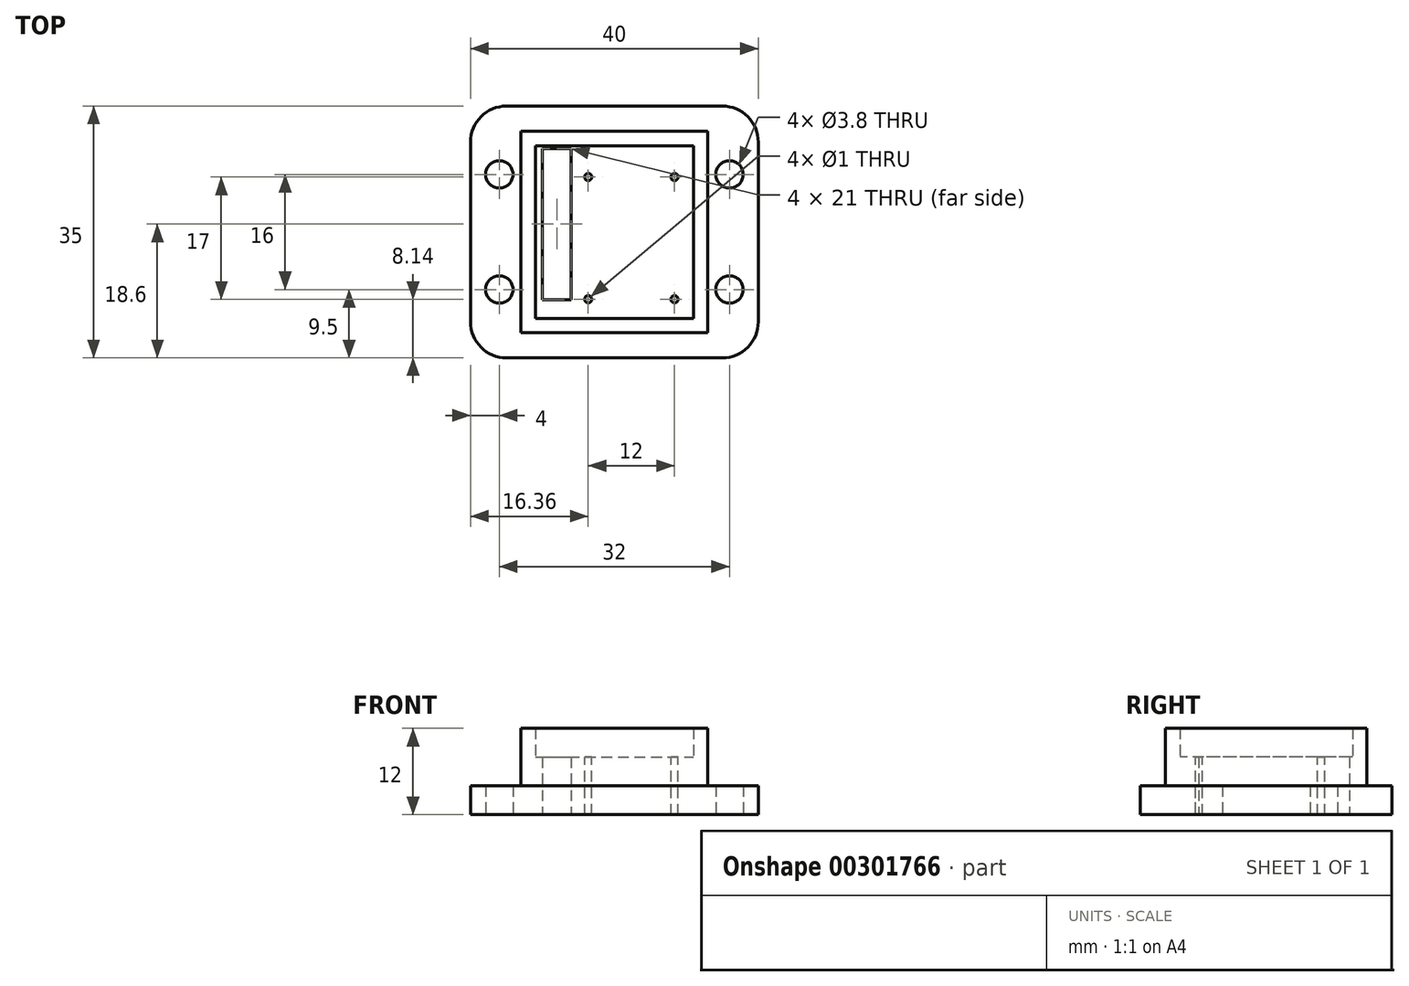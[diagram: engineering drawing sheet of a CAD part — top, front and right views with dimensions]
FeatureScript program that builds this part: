
annotation { "Feature Type Name" : "Feature", "Feature Type Description" : "" }
export const myFeature = defineFeature(function(context is Context, id is Id, definition is map)
    precondition{}
    {
        {
            var Q0;
            Q0=qCreatedBy(makeId("Top.planeOp"),FACE);
            var sketch = newSketch(context, id + "F0", { "sketchPlane" : qUnion([Q0])});
            skLineSegment(sketch, "E0.bottom", {"start": v(15, 17.5) * mm, "end": v(-15, 17.5) * mm});
            skLineSegment(sketch, "E0.top", {"start": v(15, -17.5) * mm, "end": v(-15, -17.5) * mm});
            skLineSegment(sketch, "E0.left", {"start": v(20, 12.5) * mm, "end": v(20, -12.5) * mm});
            skLineSegment(sketch, "E0.right", {"start": v(-20, 12.5) * mm, "end": v(-20, -12.5) * mm});
            skPoint(sketch, "E0.middle", {"position": v(0, 0) * mm});
            skPoint(sketch, "E1.visualSharp", {"position": v(-20, 17.5) * mm});
            skArc(sketch, "E1.filletArc", {"start": v(-15, 17.5) * mm, "mid": v(-18.54, 16.04) * mm, "end": v(-20, 12.5) * mm});
            skPoint(sketch, "E2.visualSharp", {"position": v(20, 17.5) * mm});
            skArc(sketch, "E2.filletArc", {"start": v(20, 12.5) * mm, "mid": v(18.54, 16.04) * mm, "end": v(15, 17.5) * mm});
            skPoint(sketch, "E3.visualSharp", {"position": v(-20, -17.5) * mm});
            skArc(sketch, "E3.filletArc", {"start": v(-20, -12.5) * mm, "mid": v(-18.54, -16.04) * mm, "end": v(-15, -17.5) * mm});
            skPoint(sketch, "E4.visualSharp", {"position": v(20, -17.5) * mm});
            skArc(sketch, "E4.filletArc", {"start": v(15, -17.5) * mm, "mid": v(18.54, -16.04) * mm, "end": v(20, -12.5) * mm});
            skCircle(sketch, "E5", {"center": v(16, 8) * mm, "radius": 1.9 * mm});
            skCircle(sketch, "E6", {"center": v(-16, 8) * mm, "radius": 1.9 * mm});
            skCircle(sketch, "E7", {"center": v(-16, -8) * mm, "radius": 1.9 * mm});
            skCircle(sketch, "E8", {"center": v(16, -8) * mm, "radius": 1.9 * mm});
            skLineSegment(sketch, "E9.bottom", {"start": v(-10, 11.6) * mm, "end": v(-6, 11.6) * mm});
            skLineSegment(sketch, "E9.top", {"start": v(-10, -9.4) * mm, "end": v(-6, -9.4) * mm});
            skLineSegment(sketch, "E9.left", {"start": v(-10, 11.6) * mm, "end": v(-10, -9.4) * mm});
            skLineSegment(sketch, "E9.right", {"start": v(-6, 11.6) * mm, "end": v(-6, -9.4) * mm});
            skSolve(sketch);
        }
        {
            var Q0;
            Q0 = qSketchRegion(id + "F0", true);
            extrude(context, id + "F1", {"entities" : qUnion([Q0]), "depth" : 4 * mm});
        }
        {
            var Q0;
            Q0=makeQuery(id+"F1.opExtrude","CAP_FACE",FACE,{"disambiguationData":[OSD([sQuery(id+"F0.wireOp",EDGE,"E0.bottom"),sQuery(id+"F0.wireOp",EDGE,"E0.top"),sQuery(id+"F0.wireOp",EDGE,"E0.left"),sQuery(id+"F0.wireOp",EDGE,"E0.right"),sQuery(id+"F0.wireOp",EDGE,"E1.filletArc"),sQuery(id+"F0.wireOp",EDGE,"E2.filletArc"),sQuery(id+"F0.wireOp",EDGE,"E3.filletArc"),sQuery(id+"F0.wireOp",EDGE,"E4.filletArc"),sQuery(id+"F0.wireOp",EDGE,"E5"),sQuery(id+"F0.wireOp",EDGE,"E6"),sQuery(id+"F0.wireOp",EDGE,"E7"),sQuery(id+"F0.wireOp",EDGE,"E8")])],"isStart":false});
            var sketch = newSketch(context, id + "F2", { "sketchPlane" : qUnion([Q0])});
            skLineSegment(sketch, "E10.bottom", {"start": v(13, 14) * mm, "end": v(-13, 14) * mm});
            skLineSegment(sketch, "E10.top", {"start": v(13, -14) * mm, "end": v(-13, -14) * mm});
            skLineSegment(sketch, "E10.left", {"start": v(13, 14) * mm, "end": v(13, -14) * mm});
            skLineSegment(sketch, "E10.right", {"start": v(-13, 14) * mm, "end": v(-13, -14) * mm});
            skPoint(sketch, "E10.middle", {"position": v(0, 0) * mm});
            skLineSegment(sketch, "E11.bottom", {"start": v(-11, 12) * mm, "end": v(11, 12) * mm});
            skLineSegment(sketch, "E11.top", {"start": v(-11, -12) * mm, "end": v(11, -12) * mm});
            skLineSegment(sketch, "E11.left", {"start": v(-11, 12) * mm, "end": v(-11, -12) * mm});
            skLineSegment(sketch, "E11.right", {"start": v(11, 12) * mm, "end": v(11, -12) * mm});
            skSolve(sketch);
        }
        {
            var Q0;
            Q0=makeQuery(id+"F2.imprint","IMPRINT",FACE,{"disambiguationData":[TD([[makeQuery(id+"F2.imprint","IMPRINT",EDGE,{"derivedFrom":sQuery(id+"F2.wireOp",EDGE,"E10.bottom")}),1.0]])]});
            extrude(context, id + "F3", {"entities" : qUnion([Q0]), "operationType" : NewBodyOperationType.ADD, "depth" : 8 * mm});
        }
        {
            var Q0;
            Q0=makeQuery(id+"F3.boolean.opBoolean","SPLIT",FACE,{"disambiguationData":[TD([makeQuery(id+"F3.opExtrude","SWEPT_FACE",FACE,{"disambiguationData":[OSD([sQuery(id+"F2.wireOp",EDGE,"E11.bottom")])]})])],"derivedFrom":makeQuery(id+"F1.opExtrude","CAP_FACE",FACE,{"disambiguationData":[OSD([sQuery(id+"F0.wireOp",EDGE,"E0.bottom"),sQuery(id+"F0.wireOp",EDGE,"E0.top"),sQuery(id+"F0.wireOp",EDGE,"E0.left"),sQuery(id+"F0.wireOp",EDGE,"E0.right"),sQuery(id+"F0.wireOp",EDGE,"E1.filletArc"),sQuery(id+"F0.wireOp",EDGE,"E2.filletArc"),sQuery(id+"F0.wireOp",EDGE,"E3.filletArc"),sQuery(id+"F0.wireOp",EDGE,"E4.filletArc"),sQuery(id+"F0.wireOp",EDGE,"E5"),sQuery(id+"F0.wireOp",EDGE,"E6"),sQuery(id+"F0.wireOp",EDGE,"E7"),sQuery(id+"F0.wireOp",EDGE,"E8")])],"isStart":false})});
            var sketch = newSketch(context, id + "F4", { "sketchPlane" : qUnion([Q0])});
            skCircle(sketch, "E12", {"center": v(8.36, -9.36) * mm, "radius": 1.55 * mm});
            skCircle(sketch, "E13.0.1.0", {"center": v(8.36, 7.64) * mm, "radius": 1.55 * mm});
            skCircle(sketch, "E13.1.0.0", {"center": v(-3.64, -9.36) * mm, "radius": 1.55 * mm});
            skCircle(sketch, "E13.1.1.0", {"center": v(-3.64, 7.64) * mm, "radius": 1.55 * mm});
            skLineSegment(sketch, "E13.direction1", {"start": v(8.36, -9.36) * mm, "end": v(-3.64, -9.36) * mm, "construction": true});
            skLineSegment(sketch, "E13.direction2", {"start": v(8.36, -9.36) * mm, "end": v(8.36, 7.64) * mm, "construction": true});
            skSolve(sketch);
        }
        {
            var Q0;
            Q0=sQuery(id+"F4.wireOp",VERTEX,"E13.1.0.0.center");
            var Q1;
            Q1=sQuery(id+"F4.wireOp",VERTEX,"E12.center");
            var Q2;
            Q2=sQuery(id+"F4.wireOp",VERTEX,"E13.0.1.0.center");
            var Q3;
            Q3=sQuery(id+"F4.wireOp",VERTEX,"E13.1.1.0.center");
            var Q4;
            Q4=makeQuery(id+"F1.opExtrude","SWEPT_BODY",BODY,{"disambiguationData":[OSD([sQuery(id+"F0.wireOp",EDGE,"E0.bottom"),sQuery(id+"F0.wireOp",EDGE,"E0.top"),sQuery(id+"F0.wireOp",EDGE,"E0.left"),sQuery(id+"F0.wireOp",EDGE,"E0.right"),sQuery(id+"F0.wireOp",EDGE,"E1.filletArc"),sQuery(id+"F0.wireOp",EDGE,"E2.filletArc"),sQuery(id+"F0.wireOp",EDGE,"E3.filletArc"),sQuery(id+"F0.wireOp",EDGE,"E4.filletArc"),sQuery(id+"F0.wireOp",EDGE,"E5"),sQuery(id+"F0.wireOp",EDGE,"E6"),sQuery(id+"F0.wireOp",EDGE,"E7"),sQuery(id+"F0.wireOp",EDGE,"E8")])]});
            hole(context, id + "F5", {"style" : HoleStyle.SIMPLE, "endStyle" : HoleEndStyle.THROUGH, "holeDiameter" : 1 * mm, "tappedDepth" : 12 * mm, "tapClearance" : 3, "locations" : qUnion([Q0, Q1, Q2, Q3]), "scope" : qUnion([Q4])});
        }
        {
            var Q0;
            Q0=makeQuery(id+"F3.boolean.opBoolean","SPLIT",FACE,{"disambiguationData":[TD([makeQuery(id+"F3.opExtrude","SWEPT_FACE",FACE,{"disambiguationData":[OSD([sQuery(id+"F2.wireOp",EDGE,"E11.bottom")])]})])],"derivedFrom":makeQuery(id+"F1.opExtrude","CAP_FACE",FACE,{"disambiguationData":[OSD([sQuery(id+"F0.wireOp",EDGE,"E0.bottom"),sQuery(id+"F0.wireOp",EDGE,"E0.top"),sQuery(id+"F0.wireOp",EDGE,"E0.left"),sQuery(id+"F0.wireOp",EDGE,"E0.right"),sQuery(id+"F0.wireOp",EDGE,"E1.filletArc"),sQuery(id+"F0.wireOp",EDGE,"E2.filletArc"),sQuery(id+"F0.wireOp",EDGE,"E3.filletArc"),sQuery(id+"F0.wireOp",EDGE,"E4.filletArc"),sQuery(id+"F0.wireOp",EDGE,"E5"),sQuery(id+"F0.wireOp",EDGE,"E6"),sQuery(id+"F0.wireOp",EDGE,"E7"),sQuery(id+"F0.wireOp",EDGE,"E8")])],"isStart":false})});
            var Q1;
            Q1 = qConstructionFilter(qBodyType(qCreatedBy(id + "F2" ,EDGE), BodyType.WIRE), ConstructionObject.NO);
            extrude(context, id + "F6", {"entities" : qUnion([Q0]), "operationType" : NewBodyOperationType.ADD, "surfaceEntities" : qUnion([Q1]), "depth" : 4 * mm});
        }
    });
